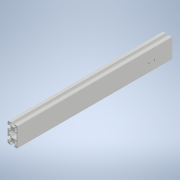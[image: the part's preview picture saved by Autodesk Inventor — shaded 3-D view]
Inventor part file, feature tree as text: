
AUTODESK INVENTOR PART (.ipt)
format: ipt  version: 2022 (Build 260153000, 153)  size: 311,808 bytes
history: native  units: mm
features: other x7, sketch x5, hole x4, pattern_linear x3, extrude x1
ambient origin geometry x8: Origin, YZ Plane, XZ Plane, XY Plane, X Axis, Y Axis, Z Axis, Center Point
bodies: Solid1 (feature_tree)
feature tree (20):
  extrude  "Extrusion1"  Depth=10.0mm TaperAngle=0.0deg
  hole  "Hole1"  [1 undecoded]
  pattern_linear  "Rectangular Pattern1"  Count1=2 Spacing1=10.0mm
  hole  "Hole2"  [1 undecoded]
  pattern_linear  "Rectangular Pattern2"  Spacing1=16.0mm  [1 undecoded]
  hole  "Hole3"  [1 undecoded]
  pattern_linear  "Rectangular Pattern3"  Spacing1=36.5mm  [1 undecoded]
  other  "C1_XY"
  other  "C1_YZ"
  other  "C1_ZX"
  other  "C1_X"
  other  "C1_Y"
  other  "C1_Z"
  other  "C1_Center"
  hole  "穴5"  [1 undecoded]
  sketch  "Sketch_63"  dims[d28=4.2mm d29=6.0mm d30=4.0mm d31=2.0mm d32=90.0deg d33=290.0mm d34=0.0mm d35=20.0mm d37=20.0mm d38=10.0mm d40=0.0mm d41=0.0mm d52=16.0mm d53=48.5mm d54=36.5mm d55=2.459mm d56=25.0mm d57=3.023mm d58=2.0mm d59=14.3117mm d60=8.8mm d61=20.594885mm]
  sketch  "Sketch2"  dims[d0=320.0mm d1=0.0mm]
  sketch  "Sketch3"  dims[d2=4.134mm d3=15.0mm d4=5.0mm d5=2.0mm d6=90.0deg d7=15.0mm d8=0.0mm d9=20.0mm d11=20.0mm d12=10.0mm d14=0.0mm]
  sketch  "Sketch4"  dims[d15=4.134mm d16=15.0mm d17=5.0mm d18=2.0mm d19=90.0deg d20=15.0mm d21=0.0mm d22=20.0mm d24=20.0mm d25=10.0mm d27=0.0mm]
  sketch  "スケッチ7"
note: 6 required parameter values undecoded (feature->parameter linkage not recoverable at this tier; creation-order binding heuristic only, values carry confidence <= 0.55)
